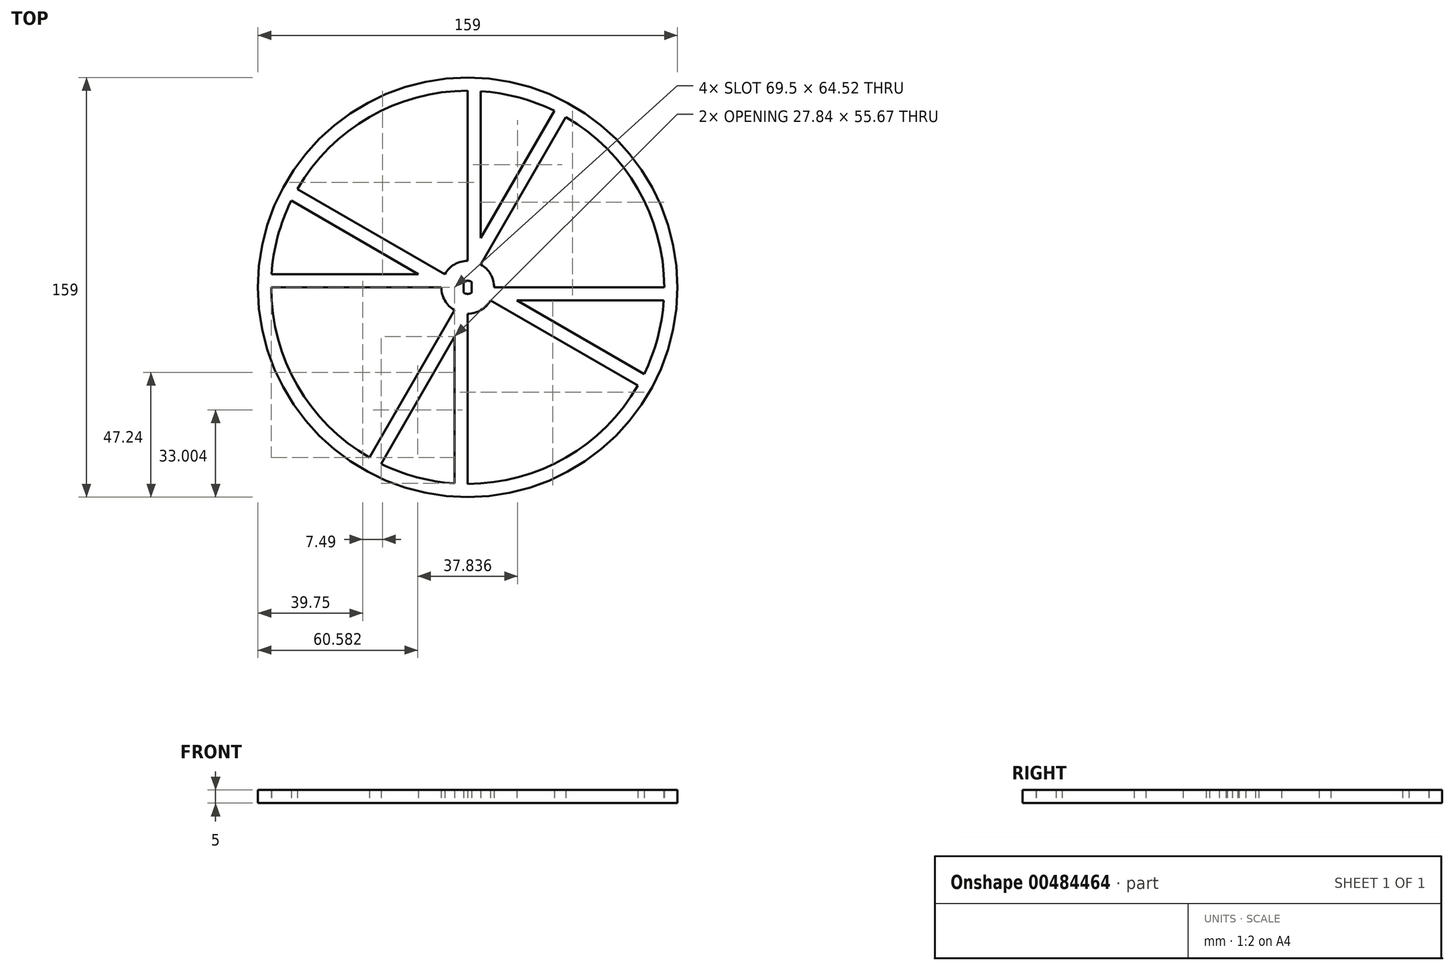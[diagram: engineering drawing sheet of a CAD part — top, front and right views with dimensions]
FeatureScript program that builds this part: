
annotation { "Feature Type Name" : "Feature", "Feature Type Description" : "" }
export const myFeature = defineFeature(function(context is Context, id is Id, definition is map)
    precondition{}
    {
        {
            var Q0;
            Q0=qCreatedBy(makeId("Top.planeOp"),FACE);
            var sketch = newSketch(context, id + "F0", { "sketchPlane" : qUnion([Q0])});
            skCircle(sketch, "E0", {"center": v(0, 0) * mm, "radius": 79.5 * mm});
            skCircle(sketch, "E1", {"center": v(0, 0) * mm, "radius": 2.5 * mm});
            skLineSegment(sketch, "E2", {"start": v(-1.5, 2) * mm, "end": v(-1.5, -2) * mm});
            skLineSegment(sketch, "E3", {"start": v(1.5, 2) * mm, "end": v(1.5, -2) * mm});
            skCircle(sketch, "E4", {"center": v(0, 0) * mm, "radius": 74.5 * mm});
            skCircle(sketch, "E5", {"center": v(0, 0) * mm, "radius": 10 * mm});
            skLineSegment(sketch, "E6", {"start": v(0, 0) * mm, "end": v(0, 79.5) * mm});
            skLineSegment(sketch, "E7", {"start": v(0, 0) * mm, "end": v(37.25, 64.52) * mm});
            skLineSegment(sketch, "E8", {"start": v(0, 0) * mm, "end": v(74.5, 0) * mm});
            skLineSegment(sketch, "E9", {"start": v(0, 0) * mm, "end": v(64.52, -37.25) * mm});
            skLineSegment(sketch, "E10", {"start": v(0, 0) * mm, "end": v(0, -74.5) * mm});
            skLineSegment(sketch, "E11", {"start": v(0, 0) * mm, "end": v(-74.5, 0) * mm});
            skLineSegment(sketch, "E12", {"start": v(0, 0) * mm, "end": v(-64.52, 37.25) * mm});
            skLineSegment(sketch, "E13", {"start": v(0, 0) * mm, "end": v(-37.25, -64.52) * mm});
            skLineSegment(sketch, "E14", {"start": v(5, 74.33) * mm, "end": v(5, 18.66) * mm});
            skLineSegment(sketch, "E15", {"start": v(5, 18.66) * mm, "end": v(32.84, 66.87) * mm});
            skLineSegment(sketch, "E16", {"start": v(74.33, -5) * mm, "end": v(18.66, -5) * mm});
            skLineSegment(sketch, "E17", {"start": v(18.66, -5) * mm, "end": v(66.87, -32.84) * mm});
            skLineSegment(sketch, "E18", {"start": v(-5, -74.33) * mm, "end": v(-5, -18.66) * mm});
            skLineSegment(sketch, "E19", {"start": v(-5, -18.66) * mm, "end": v(-32.84, -66.87) * mm});
            skLineSegment(sketch, "E20", {"start": v(-74.33, 5) * mm, "end": v(-18.66, 5) * mm});
            skLineSegment(sketch, "E21", {"start": v(-18.66, 5) * mm, "end": v(-66.87, 32.84) * mm});
            skSolve(sketch);
        }
        {
            var Q0;
            Q0=makeQuery(id+"F0.imprint","IMPRINT",FACE,{"disambiguationData":[TD([[makeQuery(id+"F0.imprint","IMPRINT",EDGE,{"derivedFrom":sQuery(id+"F0.wireOp",EDGE,"E0")}),1.0]])]});
            var Q1;
            {var subQ7=sQuery(id+"F0.wireOp",EDGE,"E20");Q1=makeQuery(id+"F0.imprint","IMPRINT",FACE,{"disambiguationData":[TD([[makeQuery(id+"F0.imprint","IMPRINT",EDGE,{"derivedFrom":subQ7}),-1.0]])]});}
            var Q2;
            {var subQ3=sQuery(id+"F0.wireOp",EDGE,"E16");Q2=makeQuery(id+"F0.imprint","IMPRINT",FACE,{"disambiguationData":[TD([[makeQuery(id+"F0.imprint","IMPRINT",EDGE,{"derivedFrom":subQ3}),-1.0]])]});}
            var Q3;
            {var subQ8=sQuery(id+"F0.wireOp",EDGE,"E18");Q3=makeQuery(id+"F0.imprint","IMPRINT",FACE,{"disambiguationData":[TD([[makeQuery(id+"F0.imprint","IMPRINT",EDGE,{"derivedFrom":subQ8}),-1.0]])]});}
            var Q4;
            {var subQ5=sQuery(id+"F0.wireOp",EDGE,"E14");Q4=makeQuery(id+"F0.imprint","IMPRINT",FACE,{"disambiguationData":[TD([[makeQuery(id+"F0.imprint","IMPRINT",EDGE,{"derivedFrom":subQ5}),-1.0]])]});}
            var Q5;
            {var subQ0=sQuery(id+"F0.wireOp",EDGE,"E8");var subQ1=sQuery(id+"F0.wireOp",EDGE,"E1");var subQ2=makeQuery(id+"F0.imprint","INTERSECT",VERTEX,{"derivedFrom":[subQ1,subQ0]});Q5=makeQuery(id+"F0.imprint","IMPRINT",FACE,{"disambiguationData":[TD([[makeQuery(id+"F0.imprint","IMPRINT",EDGE,{"disambiguationData":[TD([[subQ2,1.0]])],"derivedFrom":subQ1}),-1.0]])]});}
            var Q6;
            {var subQ5=sQuery(id+"F0.wireOp",EDGE,"E1");var subQ6=makeQuery(id+"F0.imprint","INTERSECT",VERTEX,{"disambiguationData":[OD(1.0)],"derivedFrom":[subQ5,sQuery(id+"F0.wireOp",EDGE,"E3")]});Q6=makeQuery(id+"F0.imprint","IMPRINT",FACE,{"disambiguationData":[TD([[makeQuery(id+"F0.imprint","IMPRINT",EDGE,{"disambiguationData":[TD([[subQ6,1.0]])],"derivedFrom":subQ5}),-1.0]])]});}
            var Q7;
            {var subQ5=sQuery(id+"F0.wireOp",EDGE,"E1");var subQ6=makeQuery(id+"F0.imprint","INTERSECT",VERTEX,{"disambiguationData":[OD(0.0)],"derivedFrom":[subQ5,sQuery(id+"F0.wireOp",EDGE,"E3")]});Q7=makeQuery(id+"F0.imprint","IMPRINT",FACE,{"disambiguationData":[TD([[makeQuery(id+"F0.imprint","IMPRINT",EDGE,{"disambiguationData":[TD([[subQ6,1.0]])],"derivedFrom":subQ5}),-1.0]])]});}
            var Q8;
            {var subQ0=sQuery(id+"F0.wireOp",EDGE,"E7");var subQ1=sQuery(id+"F0.wireOp",EDGE,"E1");var subQ2=makeQuery(id+"F0.imprint","INTERSECT",VERTEX,{"derivedFrom":[subQ1,subQ0]});Q8=makeQuery(id+"F0.imprint","IMPRINT",FACE,{"disambiguationData":[TD([[makeQuery(id+"F0.imprint","IMPRINT",EDGE,{"disambiguationData":[TD([[subQ2,-1.0]])],"derivedFrom":subQ1}),-1.0]])]});}
            var Q9;
            {var subQ5=sQuery(id+"F0.wireOp",EDGE,"E1");var subQ6=makeQuery(id+"F0.imprint","INTERSECT",VERTEX,{"disambiguationData":[OD(0.0)],"derivedFrom":[subQ5,sQuery(id+"F0.wireOp",EDGE,"E2")]});Q9=makeQuery(id+"F0.imprint","IMPRINT",FACE,{"disambiguationData":[TD([[makeQuery(id+"F0.imprint","IMPRINT",EDGE,{"disambiguationData":[TD([[subQ6,1.0]])],"derivedFrom":subQ5}),-1.0]])]});}
            var Q10;
            {var subQ0=sQuery(id+"F0.wireOp",EDGE,"E12");var subQ1=sQuery(id+"F0.wireOp",EDGE,"E1");var subQ2=makeQuery(id+"F0.imprint","INTERSECT",VERTEX,{"derivedFrom":[subQ1,subQ0]});Q10=makeQuery(id+"F0.imprint","IMPRINT",FACE,{"disambiguationData":[TD([[makeQuery(id+"F0.imprint","IMPRINT",EDGE,{"disambiguationData":[TD([[subQ2,-1.0]])],"derivedFrom":subQ1}),-1.0]])]});}
            var Q11;
            {var subQ5=sQuery(id+"F0.wireOp",EDGE,"E1");var subQ6=makeQuery(id+"F0.imprint","INTERSECT",VERTEX,{"disambiguationData":[OD(1.0)],"derivedFrom":[subQ5,sQuery(id+"F0.wireOp",EDGE,"E2")]});Q11=makeQuery(id+"F0.imprint","IMPRINT",FACE,{"disambiguationData":[TD([[makeQuery(id+"F0.imprint","IMPRINT",EDGE,{"disambiguationData":[TD([[subQ6,1.0]])],"derivedFrom":subQ5}),-1.0]])]});}
            var Q12;
            {var subQ0=sQuery(id+"F0.wireOp",EDGE,"E13");var subQ1=sQuery(id+"F0.wireOp",EDGE,"E1");var subQ2=makeQuery(id+"F0.imprint","INTERSECT",VERTEX,{"derivedFrom":[subQ1,subQ0]});Q12=makeQuery(id+"F0.imprint","IMPRINT",FACE,{"disambiguationData":[TD([[makeQuery(id+"F0.imprint","IMPRINT",EDGE,{"disambiguationData":[TD([[subQ2,-1.0]])],"derivedFrom":subQ1}),-1.0]])]});}
            var Q13;
            {var subQ0=sQuery(id+"F0.wireOp",EDGE,"E8");var subQ1=sQuery(id+"F0.wireOp",EDGE,"E1");var subQ2=makeQuery(id+"F0.imprint","INTERSECT",VERTEX,{"derivedFrom":[subQ1,subQ0]});Q13=makeQuery(id+"F0.imprint","IMPRINT",FACE,{"disambiguationData":[TD([[makeQuery(id+"F0.imprint","IMPRINT",EDGE,{"disambiguationData":[TD([[subQ2,1.0]])],"derivedFrom":subQ1}),1.0]])]});}
            var Q14;
            {var subQ0=sQuery(id+"F0.wireOp",EDGE,"E3");var subQ1=sQuery(id+"F0.wireOp",EDGE,"E1");var subQ2=makeQuery(id+"F0.imprint","INTERSECT",VERTEX,{"disambiguationData":[OD(0.0)],"derivedFrom":[subQ1,subQ0]});Q14=makeQuery(id+"F0.imprint","IMPRINT",FACE,{"disambiguationData":[TD([[makeQuery(id+"F0.imprint","IMPRINT",EDGE,{"disambiguationData":[TD([[subQ2,1.0]])],"derivedFrom":subQ1}),1.0]])]});}
            var Q15;
            {var subQ0=sQuery(id+"F0.wireOp",EDGE,"E3");var subQ1=sQuery(id+"F0.wireOp",EDGE,"E1");var subQ2=makeQuery(id+"F0.imprint","INTERSECT",VERTEX,{"disambiguationData":[OD(1.0)],"derivedFrom":[subQ1,subQ0]});Q15=makeQuery(id+"F0.imprint","IMPRINT",FACE,{"disambiguationData":[TD([[makeQuery(id+"F0.imprint","IMPRINT",EDGE,{"disambiguationData":[TD([[subQ2,-1.0]])],"derivedFrom":subQ1}),1.0]])]});}
            var Q16;
            {var subQ0=sQuery(id+"F0.wireOp",EDGE,"E2");var subQ1=sQuery(id+"F0.wireOp",EDGE,"E1");var subQ2=makeQuery(id+"F0.imprint","INTERSECT",VERTEX,{"disambiguationData":[OD(1.0)],"derivedFrom":[subQ1,subQ0]});Q16=makeQuery(id+"F0.imprint","IMPRINT",FACE,{"disambiguationData":[TD([[makeQuery(id+"F0.imprint","IMPRINT",EDGE,{"disambiguationData":[TD([[subQ2,1.0]])],"derivedFrom":subQ1}),1.0]])]});}
            var Q17;
            {var subQ0=sQuery(id+"F0.wireOp",EDGE,"E12");var subQ1=sQuery(id+"F0.wireOp",EDGE,"E1");var subQ2=makeQuery(id+"F0.imprint","INTERSECT",VERTEX,{"derivedFrom":[subQ1,subQ0]});Q17=makeQuery(id+"F0.imprint","IMPRINT",FACE,{"disambiguationData":[TD([[makeQuery(id+"F0.imprint","IMPRINT",EDGE,{"disambiguationData":[TD([[subQ2,-1.0]])],"derivedFrom":subQ1}),1.0]])]});}
            var Q18;
            {var subQ0=sQuery(id+"F0.wireOp",EDGE,"E2");var subQ1=sQuery(id+"F0.wireOp",EDGE,"E1");var subQ2=makeQuery(id+"F0.imprint","INTERSECT",VERTEX,{"disambiguationData":[OD(0.0)],"derivedFrom":[subQ1,subQ0]});Q18=makeQuery(id+"F0.imprint","IMPRINT",FACE,{"disambiguationData":[TD([[makeQuery(id+"F0.imprint","IMPRINT",EDGE,{"disambiguationData":[TD([[subQ2,-1.0]])],"derivedFrom":subQ1}),1.0]])]});}
            extrude(context, id + "F1", {"entities" : qUnion([Q0, Q1, Q2, Q3, Q4, Q5, Q6, Q7, Q8, Q9, Q10, Q11, Q12, Q13, Q14, Q15, Q16, Q17, Q18]), "depth" : 5 * mm});
        }
    });
